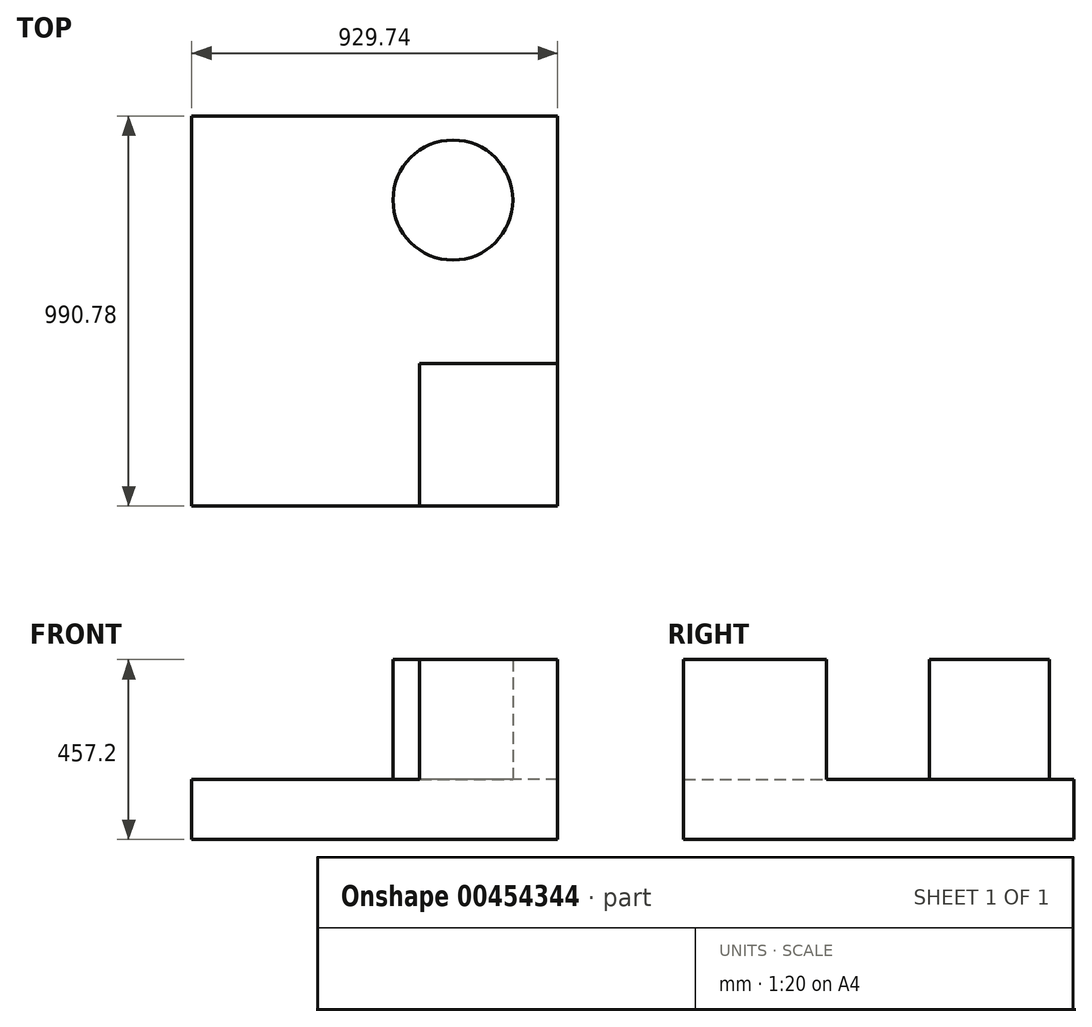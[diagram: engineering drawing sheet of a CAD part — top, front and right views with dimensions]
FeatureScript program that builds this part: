
annotation { "Feature Type Name" : "Feature", "Feature Type Description" : "" }
export const myFeature = defineFeature(function(context is Context, id is Id, definition is map)
    precondition{}
    {
        {
            var Q0;
            Q0=qCreatedBy(makeId("Top.planeOp"),FACE);
            var sketch = newSketch(context, id + "F0", { "sketchPlane" : qUnion([Q0])});
            skLineSegment(sketch, "E0.bottom", {"start": v(-406.7, -249.83) * mm, "end": v(523.04, -249.83) * mm});
            skLineSegment(sketch, "E0.top", {"start": v(-406.7, -1240.6) * mm, "end": v(523.04, -1240.6) * mm});
            skLineSegment(sketch, "E0.left", {"start": v(-406.7, -249.83) * mm, "end": v(-406.7, -1240.6) * mm});
            skLineSegment(sketch, "E0.right", {"start": v(523.04, -249.83) * mm, "end": v(523.04, -1240.6) * mm});
            skSolve(sketch);
        }
        {
            var Q0;
            Q0=qSketchRegion(id+"F0",true);
            extrude(context, id + "F1", {"entities" : qUnion([Q0]), "depth" : 152.4 * mm});
        }
        {
            var Q0;
            Q0=makeQuery(id+"F1.opExtrude","CAP_FACE",FACE,{"disambiguationData":[OSD([sQuery(id+"F0.wireOp",EDGE,"E0.bottom"),sQuery(id+"F0.wireOp",EDGE,"E0.top"),sQuery(id+"F0.wireOp",EDGE,"E0.left"),sQuery(id+"F0.wireOp",EDGE,"E0.right")])],"isStart":false});
            var sketch = newSketch(context, id + "F2", { "sketchPlane" : qUnion([Q0])});
            skCircle(sketch, "E1", {"center": v(256.94, -463.3) * mm, "radius": 152.4 * mm});
            skSolve(sketch);
        }
        {
            var Q0;
            Q0=makeQuery(id+"F2.imprint","IMPRINT",FACE,{"disambiguationData":[TD([[makeQuery(id+"F2.imprint","IMPRINT",EDGE,{"derivedFrom":sQuery(id+"F2.wireOp",EDGE,"E1")}),1.0]])]});
            extrude(context, id + "F3", {"entities" : qUnion([Q0]), "depth" : 304.8 * mm});
        }
        {
            var Q0;
            Q0=makeQuery(id+"F1.opExtrude","CAP_FACE",FACE,{"disambiguationData":[OSD([sQuery(id+"F0.wireOp",EDGE,"E0.bottom"),sQuery(id+"F0.wireOp",EDGE,"E0.top"),sQuery(id+"F0.wireOp",EDGE,"E0.left"),sQuery(id+"F0.wireOp",EDGE,"E0.right")])],"isStart":false});
            var sketch = newSketch(context, id + "F4", { "sketchPlane" : qUnion([Q0])});
            skLineSegment(sketch, "E2.bottom", {"start": v(523.04, -1240.6) * mm, "end": v(171.98, -1240.6) * mm});
            skLineSegment(sketch, "E2.top", {"start": v(523.04, -878.02) * mm, "end": v(171.98, -878.02) * mm});
            skLineSegment(sketch, "E2.left", {"start": v(523.04, -1240.6) * mm, "end": v(523.04, -878.02) * mm});
            skLineSegment(sketch, "E2.right", {"start": v(171.98, -1240.6) * mm, "end": v(171.98, -878.02) * mm});
            skSolve(sketch);
        }
        {
            var Q0;
            Q0=qSketchRegion(id+"F4",true);
            extrude(context, id + "F5", {"entities" : qUnion([Q0]), "operationType" : NewBodyOperationType.ADD, "depth" : 304.8 * mm});
        }
    });
